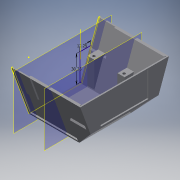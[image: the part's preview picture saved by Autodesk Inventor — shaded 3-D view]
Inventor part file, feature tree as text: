
AUTODESK INVENTOR PART (.ipt)
format: ipt  version: 2017 (Build 210142000, 142)  size: 269,312 bytes
history: native  units: mm
features: sketch x9, extrude x7, plane x4, mirror x2, draft x1, fillet x1, other x1, chamfer x1, shell x1, projected_geometry x1
ambient origin geometry x8: Origin, YZ Plane, XZ Plane, XY Plane, X Axis, Y Axis, Z Axis, Center Point
bodies: Solid1 (feature_tree)
feature tree (28):
  extrude  "Extrusion1"  Depth=55.0mm
  draft  "FaceDraft1"
  fillet  "Fillet1"  Radius=31.0mm
  extrude  "Extrusion2"  Depth=78.0mm TaperAngle=0.0deg
  other  "Midplane"
  mirror  "Mirror1"
  extrude  "Extrusion3"  Depth=3.0mm
  extrude  "Extrusion5"  Depth=1.5mm TaperAngle=0.0deg
  extrude  "Extrusion6"  Depth=53.75mm
  chamfer  "Chamfer2"  Distance=53.75mm
  shell  "Shell1"  Thickness=1.75mm
  sketch  "Sketch7"  dims[d23=27.5mm]
  plane  "Work Plane5"
  extrude  "Extrusion7"  Depth=1.5mm TaperAngle=0.0deg
  extrude  "Extrusion8"  Depth=27.5mm
  mirror  "Mirror2"
  sketch  "Sketch12"  dims[d26=27.5mm d27=53.75mm d28=1.75mm d29=1.5mm d30=0.0mm d31=27.5mm d32=53.75mm d33=2.0mm d34=1.5mm d35=0.0mm d39=1.5mm d40=2.0mm d41=45.0deg d43=-8.25mm d44=-34.0mm d45=30.25mm d46=13.0mm d47=8.0mm d48=0.0mm d49=8.0mm d50=0.0mm]
  sketch  "Sketch1"  dims[d0=55.0mm d1=57.0mm d3=31.0mm]
  sketch  "Sketch2"  dims[d5=78.0mm d6=60.0mm d7=0.0mm]
  plane  "Work Plane1"
  plane  "Work Plane2"
  sketch  "Sketch3"  dims[d8=3.490659mm d9=3.0mm]
  sketch  "Sketch5"  dims[d10=1.5mm d13=1.5mm d14=0.0mm]
  sketch  "Sketch6"  dims[d17=1.5mm d18=0.0mm d22=53.75mm]
  plane  "Work Plane4"
  sketch  "Sketch9"  dims[d24=27.5mm]
  sketch  "Sketch10"  dims[d25=53.75mm]
  projected_geometry  "Projected Loop2"
